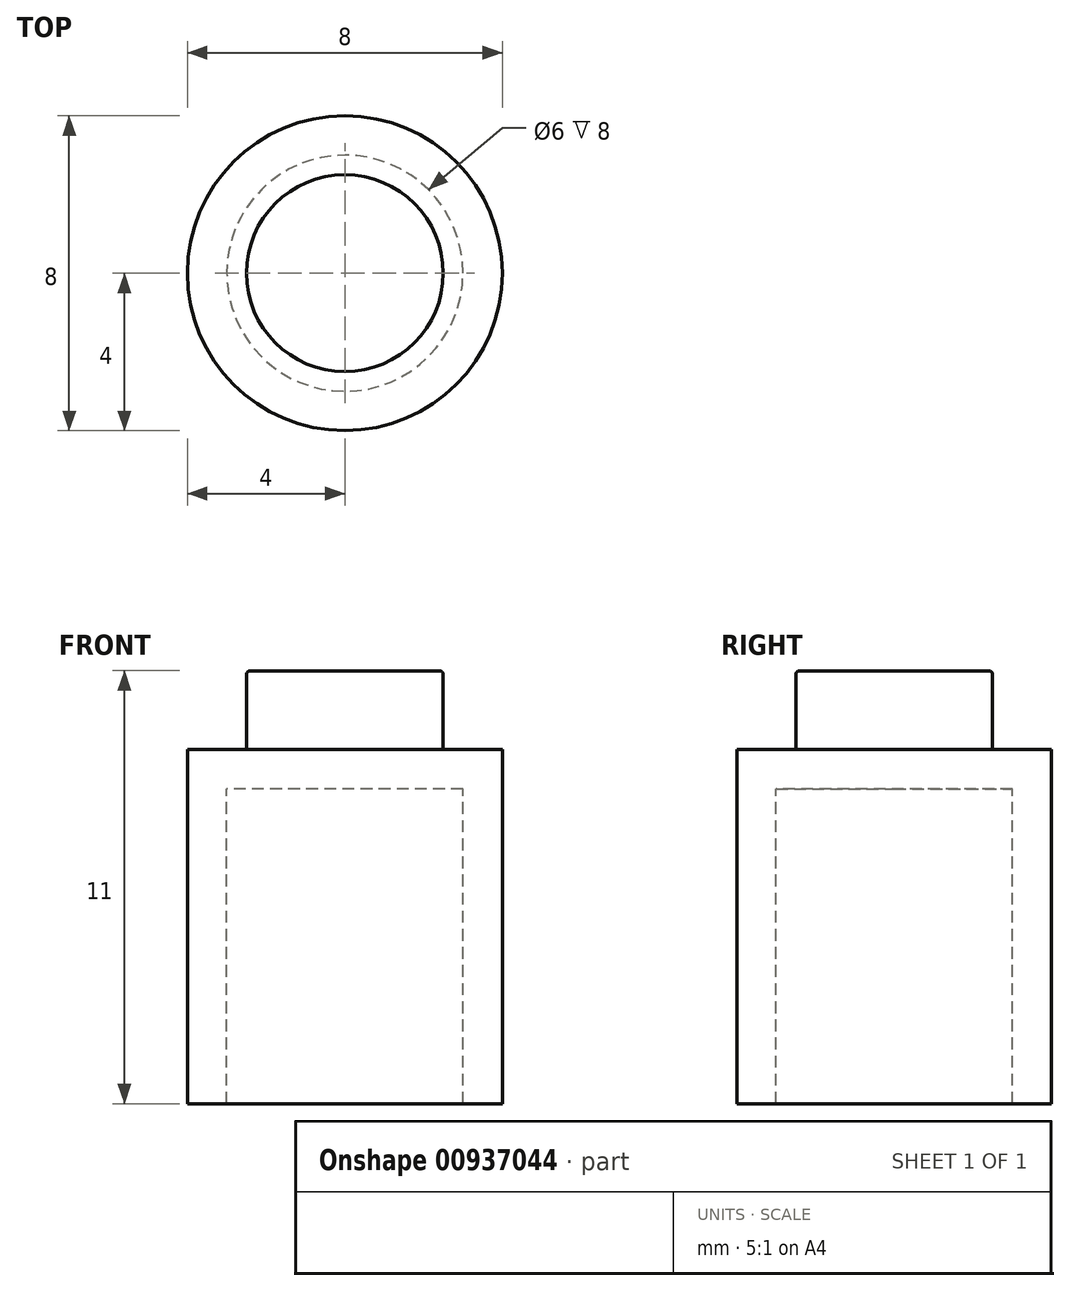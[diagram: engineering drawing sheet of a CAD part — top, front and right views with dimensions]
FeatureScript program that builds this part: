
annotation { "Feature Type Name" : "Feature", "Feature Type Description" : "" }
export const myFeature = defineFeature(function(context is Context, id is Id, definition is map)
    precondition{}
    {
        {
            var Q0;
            Q0=qCreatedBy(makeId("Front.planeOp"),FACE);
            var sketch = newSketch(context, id + "F0", { "sketchPlane" : qUnion([Q0])});
            skLineSegment(sketch, "E0.bottom", {"start": v(0, 4.24) * mm, "end": v(4, 4.24) * mm});
            skLineSegment(sketch, "E0.right", {"start": v(4, 4.24) * mm, "end": v(4, -4.76) * mm});
            skLineSegment(sketch, "E1.bottom", {"start": v(0, 6.24) * mm, "end": v(2.5, 6.24) * mm});
            skLineSegment(sketch, "E1.top", {"start": v(0, 4.24) * mm, "end": v(2.5, 4.24) * mm});
            skLineSegment(sketch, "E1.left", {"start": v(0, 6.24) * mm, "end": v(0, 4.24) * mm});
            skLineSegment(sketch, "E1.right", {"start": v(2.5, 6.24) * mm, "end": v(2.5, 4.24) * mm});
            skLineSegment(sketch, "E2", {"start": v(3, -4.76) * mm, "end": v(3, 3.24) * mm});
            skLineSegment(sketch, "E3", {"start": v(3, 3.24) * mm, "end": v(0, 3.24) * mm});
            skLineSegment(sketch, "E4", {"start": v(3, -4.76) * mm, "end": v(4, -4.76) * mm});
            skLineSegment(sketch, "E5", {"start": v(0, 4.24) * mm, "end": v(0, 3.24) * mm});
            skSolve(sketch);
        }
        {
            var Q0;
            Q0=qCreatedBy(makeId("Front.planeOp"),FACE);
            var sketch = newSketch(context, id + "F1", { "sketchPlane" : qUnion([Q0])});
            skSolve(sketch);
        }
        {
            var Q0;
            Q0 = qSketchRegion(id + "F1", true);
            var Q1;
            {var subQ0=sQuery(id+"F0.wireOp",EDGE,"E0.right");Q1=makeQuery(id+"F0.imprint","IMPRINT",FACE,{"disambiguationData":[TD([[makeQuery(id+"F0.imprint","IMPRINT",EDGE,{"derivedFrom":subQ0}),-1.0]])]});}
            var Q2;
            Q2=makeQuery(id+"F0.imprint","IMPRINT",FACE,{"disambiguationData":[TD([[makeQuery(id+"F0.imprint","IMPRINT",EDGE,{"derivedFrom":sQuery(id+"F0.wireOp",EDGE,"E1.bottom")}),-1.0]])]});
            var Q3;
            Q3=sQuery(id+"F0.wireOp",EDGE,"E5");
            revolve(context, id + "F2", {"surfaceOperationType" : NewSurfaceOperationType.NEW, "entities" : qUnion([Q0, Q1, Q2]), "axis" : qUnion([Q3]), "revolveType" : RevolveType.FULL});
        }
        {
            var Q0;
            Q0=makeQuery(id+"F2.opRevolve","SWEPT_FACE",FACE,{"disambiguationData":[OSD([sQuery(id+"F0.wireOp",EDGE,"E1.bottom")])]});
            fillet(context, id + "F3", {"entities" : qUnion([Q0]), "radius" : 0.1 * mm, "tangentPropagation" : true, "allowEdgeOverflow" : false});
        }
    });
